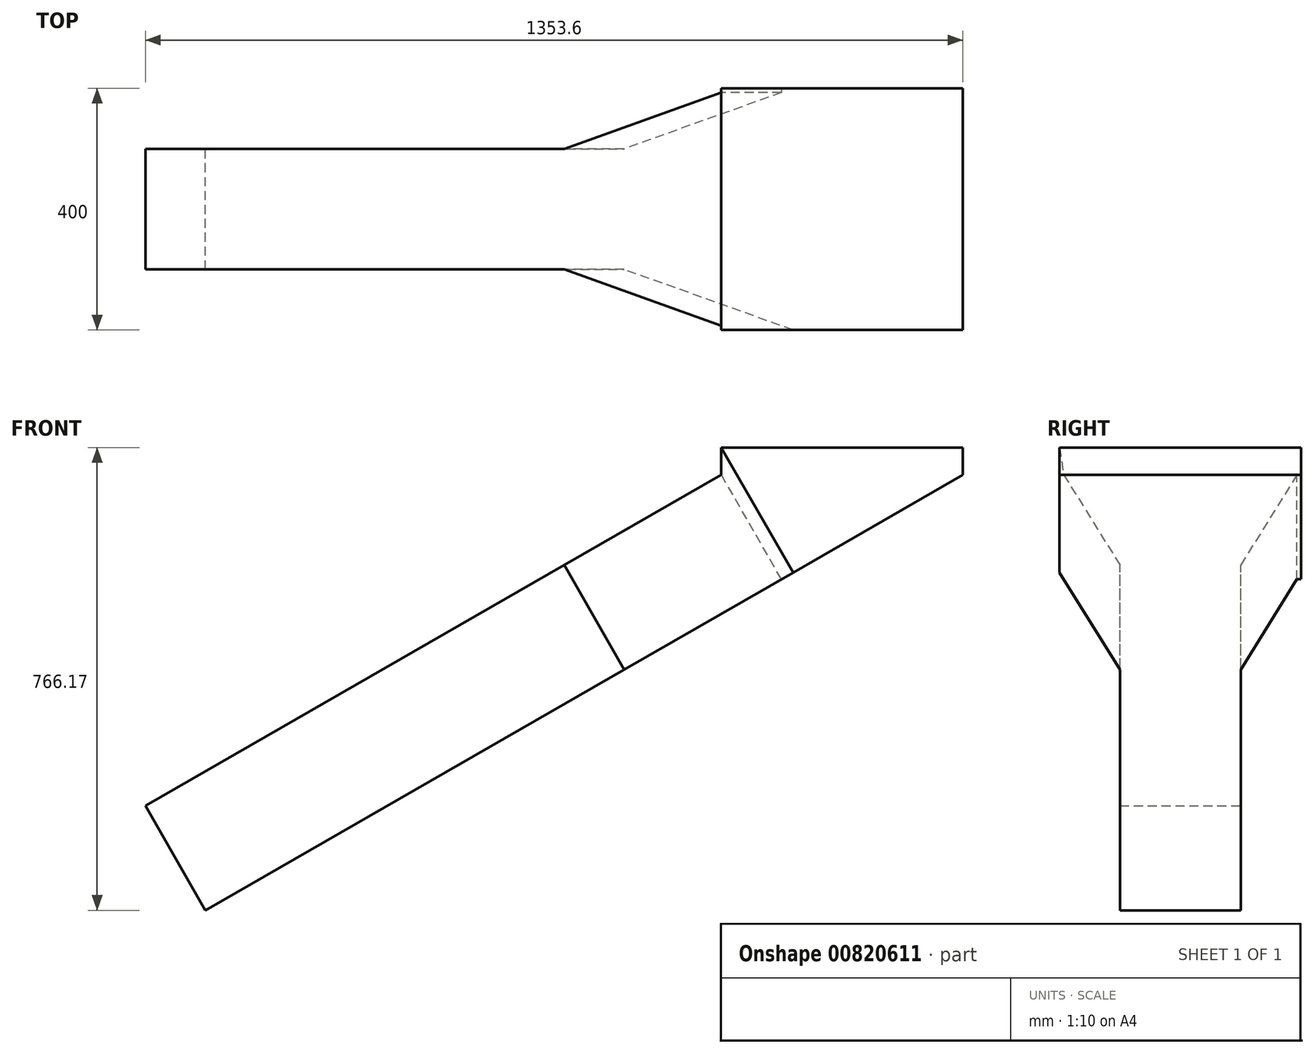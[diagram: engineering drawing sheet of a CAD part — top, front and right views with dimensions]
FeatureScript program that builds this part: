
annotation { "Feature Type Name" : "Feature", "Feature Type Description" : "" }
export const myFeature = defineFeature(function(context is Context, id is Id, definition is map)
    precondition{}
    {
        {
            var Q0;
            Q0=qCreatedBy(makeId("Front.planeOp"),FACE);
            var sketch = newSketch(context, id + "F0", { "sketchPlane" : qUnion([Q0])});
            skLineSegment(sketch, "E0", {"start": v(0, 151.86) * mm, "end": v(400, 151.86) * mm});
            skLineSegment(sketch, "E1", {"start": v(400, 151.86) * mm, "end": v(400, 106.86) * mm});
            skLineSegment(sketch, "E2", {"start": v(0, 151.86) * mm, "end": v(0, 106.86) * mm});
            skLineSegment(sketch, "E3", {"start": v(0, 106.86) * mm, "end": v(-260.07, -42.69) * mm});
            skLineSegment(sketch, "E4", {"start": v(400, 106.86) * mm, "end": v(-813.67, -591) * mm});
            skLineSegment(sketch, "E5", {"start": v(0, 0) * mm, "end": v(788.78, 0) * mm, "construction": true});
            skLineSegment(sketch, "E6", {"start": v(0, 106.86) * mm, "end": v(0, -184.1) * mm, "construction": true});
            skPoint(sketch, "E7", {"position": v(0, -123.14) * mm});
            skLineSegment(sketch, "E8", {"start": v(-813.67, -591) * mm, "end": v(-913.36, -417.62) * mm});
            skLineSegment(sketch, "E9", {"start": v(-913.36, -417.62) * mm, "end": v(-260.07, -42.69) * mm});
            skLineSegment(sketch, "E10", {"start": v(-260.07, -42.69) * mm, "end": v(-160.68, -215.54) * mm});
            skSolve(sketch);
        }
        {
            var Q0;
            Q0=makeQuery(id+"F0.imprint","IMPRINT",FACE,{"disambiguationData":[TD([[makeQuery(id+"F0.imprint","IMPRINT",EDGE,{"derivedFrom":sQuery(id+"F0.wireOp",EDGE,"E0")}),-1.0]])]});
            extrude(context, id + "F1", {"entities" : qUnion([Q0]), "depth" : 400 * mm, "offsetDistance" : 25 * mm});
        }
        {
            var Q0;
            Q0=makeQuery(id+"F1.opExtrude","SWEPT_FACE",FACE,{"disambiguationData":[OSD([sQuery(id+"F0.wireOp",EDGE,"E3")])]});
            var sketch = newSketch(context, id + "F2", { "sketchPlane" : qUnion([Q0])});
            skLineSegment(sketch, "E11", {"start": v(422.46, -200) * mm, "end": v(-433.55, -200) * mm, "construction": true});
            skLineSegment(sketch, "E12", {"start": v(-246.74, -100) * mm, "end": v(75.7, 0) * mm});
            skLineSegment(sketch, "E13.MirrorCS", {"start": v(-246.74, -300) * mm, "end": v(75.7, -400) * mm});
            skPoint(sketch, "E14", {"position": v(-232.2, -95.5) * mm});
            skPoint(sketch, "E15", {"position": v(-261.27, -295.5) * mm});
            skLineSegment(sketch, "E16.0", {"start": v(-246.74, -300) * mm, "end": v(-246.74, -100) * mm});
            skLineSegment(sketch, "E17.0.1", {"start": v(-246.74, -100) * mm, "end": v(-246.74, -300) * mm});
            skPoint(sketch, "E17.0.0.end.orphan", {"position": v(-246.74, 0) * mm});
            skPoint(sketch, "E18.orphan", {"position": v(-246.74, -400) * mm});
            skLineSegment(sketch, "E19", {"start": v(-246.74, -100) * mm, "end": v(-246.74, 0) * mm});
            skLineSegment(sketch, "E20", {"start": v(-246.74, -300) * mm, "end": v(-246.74, -400) * mm});
            skLineSegment(sketch, "E21", {"start": v(75.7, -400) * mm, "end": v(-246.74, -400) * mm});
            skSolve(sketch);
        }
        {
            var Q0;
            Q0 = qSketchRegion(id + "F2", true);
            var Q1;
            {var subQ0=sQuery(id+"F2.wireOp",EDGE,"E19");Q1=makeQuery(id+"F2.imprint","IMPRINT",FACE,{"disambiguationData":[TD([[makeQuery(id+"F2.imprint","IMPRINT",EDGE,{"derivedFrom":subQ0}),-1.0]])]});}
            extrude(context, id + "F3", {"entities" : qUnion([Q0, Q1]), "operationType" : NewBodyOperationType.REMOVE, "endBound" : BoundingType.SYMMETRIC, "oppositeDirection" : true, "depth" : 1000 * mm, "offsetDistance" : 25 * mm});
        }
        {
            var Q0;
            Q0=makeQuery(id+"F1.opExtrude","SWEPT_FACE",FACE,{"disambiguationData":[OSD([sQuery(id+"F0.wireOp",EDGE,"E10")])]});
            var sketch = newSketch(context, id + "F4", { "sketchPlane" : qUnion([Q0])});
            skLineSegment(sketch, "E22.0", {"start": v(300, 92.63) * mm, "end": v(100, 92.63) * mm});
            skPoint(sketch, "E23.0", {"position": v(300, -7.06) * mm});
            skLineSegment(sketch, "E24.0", {"start": v(300, -106.76) * mm, "end": v(100, -106.76) * mm});
            skLineSegment(sketch, "E25.0", {"start": v(100, -106.76) * mm, "end": v(100, 92.63) * mm});
            skSolve(sketch);
        }
        {
            var Q0;
            Q0=makeQuery(id+"F4.imprint","IMPRINT",FACE,{"disambiguationData":[TD([[makeQuery(id+"F4.imprint","IMPRINT",EDGE,{"derivedFrom":sQuery(id+"F4.wireOp",EDGE,"E22.0")}),1.0]])]});
            extrude(context, id + "F5", {"entities" : qUnion([Q0]), "operationType" : NewBodyOperationType.ADD, "depth" : 800 * mm, "offsetDistance" : 25 * mm});
        }
    });
